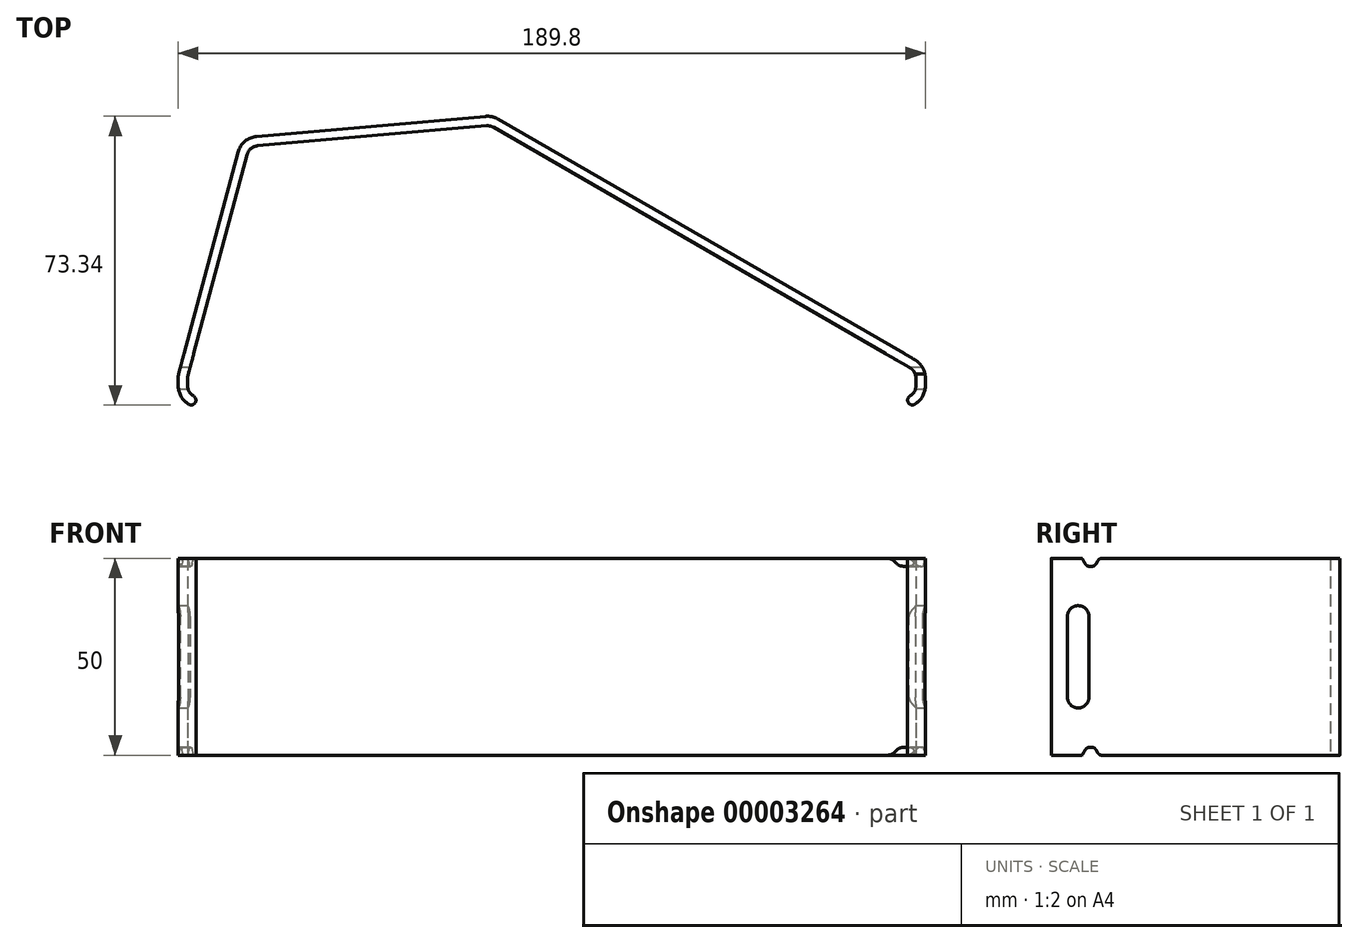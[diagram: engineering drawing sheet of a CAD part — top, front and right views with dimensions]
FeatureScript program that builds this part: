
annotation { "Feature Type Name" : "Feature", "Feature Type Description" : "" }
export const myFeature = defineFeature(function(context is Context, id is Id, definition is map)
    precondition{}
    {
        {
            var Q0;
            Q0=qCreatedBy(makeId("Top.planeOp"),FACE);
            var sketch = newSketch(context, id + "F0", { "sketchPlane" : qUnion([Q0])});
            skLineSegment(sketch, "E0", {"start": v(-74.96, 62.4) * mm, "end": v(-16.8, 67.48) * mm});
            skLineSegment(sketch, "E1", {"start": v(-13.63, 66.78) * mm, "end": v(92.2, 5.68) * mm});
            skLineSegment(sketch, "E2", {"start": v(94.9, 1) * mm, "end": v(94.9, -1) * mm});
            skLineSegment(sketch, "E3", {"start": v(92.5, -1) * mm, "end": v(92.5, 1) * mm});
            skLineSegment(sketch, "E4", {"start": v(91, 3.6) * mm, "end": v(-14.83, 64.7) * mm});
            skLineSegment(sketch, "E5", {"start": v(-16.59, 65.09) * mm, "end": v(-74.75, 60) * mm});
            skLineSegment(sketch, "E6", {"start": v(-77.39, 57.79) * mm, "end": v(-92.4, 1.78) * mm});
            skLineSegment(sketch, "E7", {"start": v(-92.5, 1) * mm, "end": v(-92.5, -1) * mm});
            skLineSegment(sketch, "E8", {"start": v(-94.9, -1) * mm, "end": v(-94.9, 1) * mm});
            skLineSegment(sketch, "E9", {"start": v(-94.72, 2.4) * mm, "end": v(-79.7, 58.4) * mm});
            skPoint(sketch, "E10.visualSharp", {"position": v(-15.1, 67.63) * mm});
            skPoint(sketch, "E11.visualSharp", {"position": v(94.9, 4.12) * mm});
            skArc(sketch, "E11.filletArc", {"start": v(94.9, 1) * mm, "mid": v(94.18, 3.7) * mm, "end": v(92.2, 5.68) * mm});
            skPoint(sketch, "E12.visualSharp", {"position": v(94.9, -8) * mm});
            skArc(sketch, "E12.filletArc", {"start": v(92.2, -5.68) * mm, "mid": v(94.18, -3.7) * mm, "end": v(94.9, -1) * mm});
            skPoint(sketch, "E13.visualSharp", {"position": v(-94.9, -5.56) * mm});
            skArc(sketch, "E13.filletArc", {"start": v(-94.9, -1) * mm, "mid": v(-94.18, -3.7) * mm, "end": v(-92.2, -5.68) * mm});
            skPoint(sketch, "E14.visualSharp", {"position": v(-94.9, 1.71) * mm});
            skArc(sketch, "E14.filletArc", {"start": v(-94.72, 2.4) * mm, "mid": v(-94.85, 1.7) * mm, "end": v(-94.9, 1) * mm});
            skPoint(sketch, "E15.visualSharp", {"position": v(-78.73, 62.06) * mm});
            skArc(sketch, "E15.filletArc", {"start": v(-74.96, 62.4) * mm, "mid": v(-77.96, 61.15) * mm, "end": v(-79.7, 58.4) * mm});
            skPoint(sketch, "E16.visualSharp", {"position": v(-15.65, 65.17) * mm});
            skArc(sketch, "E16.filletArc", {"start": v(-14.83, 64.7) * mm, "mid": v(-15.68, 65.03) * mm, "end": v(-16.59, 65.09) * mm});
            skPoint(sketch, "E17.visualSharp", {"position": v(-76.85, 59.82) * mm});
            skArc(sketch, "E17.filletArc", {"start": v(-74.75, 60) * mm, "mid": v(-76.42, 59.3) * mm, "end": v(-77.39, 57.79) * mm});
            skPoint(sketch, "E18.visualSharp", {"position": v(-92.5, 1.4) * mm});
            skArc(sketch, "E18.filletArc", {"start": v(-92.4, 1.78) * mm, "mid": v(-92.47, 1.4) * mm, "end": v(-92.5, 1) * mm});
            skPoint(sketch, "E19.visualSharp", {"position": v(92.5, 2.73) * mm});
            skArc(sketch, "E19.filletArc", {"start": v(92.5, 1) * mm, "mid": v(92.1, 2.5) * mm, "end": v(91, 3.6) * mm});
            skPoint(sketch, "E20.visualSharp", {"position": v(92.5, -2.9) * mm});
            skArc(sketch, "E20.filletArc", {"start": v(91, -3.6) * mm, "mid": v(92.1, -2.5) * mm, "end": v(92.5, -1) * mm});
            skPoint(sketch, "E21.visualSharp", {"position": v(-92.5, -3) * mm});
            skArc(sketch, "E21.filletArc", {"start": v(-92.5, -1) * mm, "mid": v(-92.1, -2.5) * mm, "end": v(-91, -3.6) * mm});
            skLineSegment(sketch, "E22", {"start": v(92.5, 0) * mm, "end": v(-92.5, 0) * mm, "construction": true});
            skArc(sketch, "E23", {"start": v(-92.2, -5.68) * mm, "mid": v(-90.56, -5.24) * mm, "end": v(-91, -3.6) * mm});
            skArc(sketch, "E24", {"start": v(91, -3.6) * mm, "mid": v(90.56, -5.24) * mm, "end": v(92.2, -5.68) * mm});
            skArc(sketch, "E25", {"start": v(-13.63, 66.78) * mm, "mid": v(-15.16, 67.37) * mm, "end": v(-16.8, 67.48) * mm});
            skLineSegment(sketch, "E26", {"start": v(-89.5, -1) * mm, "end": v(-91.6, -4.64) * mm, "construction": true});
            skLineSegment(sketch, "E27", {"start": v(89.5, -1) * mm, "end": v(91.6, -4.64) * mm, "construction": true});
            skSolve(sketch);
        }
        {
            var Q0;
            Q0 = qSketchRegion(id + "F0", true);
            extrude(context, id + "F1", {"entities" : qUnion([Q0]), "endBound" : BoundingType.SYMMETRIC, "depth" : 50 * mm});
        }
        {
            var Q0;
            Q0=qCreatedBy(makeId("Right.planeOp"),FACE);
            var sketch = newSketch(context, id + "F2", { "sketchPlane" : qUnion([Q0])});
            skLineSegment(sketch, "E28", {"start": v(3.75, 10.25) * mm, "end": v(3.75, -10.25) * mm});
            skLineSegment(sketch, "E29", {"start": v(-1.75, 10.25) * mm, "end": v(-1.75, -10.25) * mm});
            skArc(sketch, "E30", {"start": v(3.75, 10.25) * mm, "mid": v(1, 13) * mm, "end": v(-1.75, 10.25) * mm});
            skArc(sketch, "E31", {"start": v(3.75, -10.25) * mm, "mid": v(1, -13) * mm, "end": v(-1.75, -10.25) * mm});
            skLineSegment(sketch, "E32", {"start": v(1, 10.25) * mm, "end": v(1, -10.25) * mm, "construction": true});
            skLineSegment(sketch, "E33", {"start": v(1, 0) * mm, "end": v(0, 0) * mm, "construction": true});
            skLineSegment(sketch, "E34", {"start": v(1, 13) * mm, "end": v(1, 25) * mm, "construction": true});
            skSolve(sketch);
        }
        {
            var Q0;
            Q0 = qSketchRegion(id + "F2", true);
            extrude(context, id + "F3", {"entities" : qUnion([Q0]), "operationType" : NewBodyOperationType.REMOVE, "endBound" : BoundingType.THROUGH_ALL, "oppositeDirection" : true, "depth" : 25 * mm, "hasSecondDirection" : true, "secondDirectionBound" : SecondDirectionBoundingType.THROUGH_ALL, "secondDirectionOppositeDirection" : false, "secondDirectionDepth" : 25 * mm});
        }
        {
            var Q0;
            Q0=qCreatedBy(makeId("Right.planeOp"),FACE);
            var sketch = newSketch(context, id + "F4", { "sketchPlane" : qUnion([Q0])});
            skLineSegment(sketch, "E35", {"start": v(2, 25) * mm, "end": v(2, 25) * mm});
            skLineSegment(sketch, "E36", {"start": v(2, 25) * mm, "end": v(3.15, 23) * mm});
            skLineSegment(sketch, "E37", {"start": v(3.15, 23) * mm, "end": v(5.15, 23) * mm});
            skLineSegment(sketch, "E38", {"start": v(5.15, 23) * mm, "end": v(6.3, 25) * mm});
            skLineSegment(sketch, "E39", {"start": v(6.3, 25) * mm, "end": v(2, 25) * mm});
            skLineSegment(sketch, "E40", {"start": v(0, 0) * mm, "end": v(-15.35, 0) * mm, "construction": true});
            skLineSegment(sketch, "E41.MirrorCS", {"start": v(6.3, -25) * mm, "end": v(2, -25) * mm});
            skLineSegment(sketch, "E42.MirrorCS", {"start": v(3.15, -23) * mm, "end": v(5.15, -23) * mm});
            skLineSegment(sketch, "E43.MirrorCS", {"start": v(5.15, -23) * mm, "end": v(6.3, -25) * mm});
            skLineSegment(sketch, "E44.MirrorCS", {"start": v(2, -25) * mm, "end": v(2, -25) * mm});
            skLineSegment(sketch, "E45.MirrorCS", {"start": v(2, -25) * mm, "end": v(3.15, -23) * mm});
            skLineSegment(sketch, "E46", {"start": v(0, 0) * mm, "end": v(2, 0) * mm, "construction": true});
            skLineSegment(sketch, "E47", {"start": v(2, 25) * mm, "end": v(2, -25) * mm, "construction": true});
            skSolve(sketch);
        }
        {
            var Q0;
            Q0 = qSketchRegion(id + "F4", true);
            extrude(context, id + "F5", {"entities" : qUnion([Q0]), "operationType" : NewBodyOperationType.REMOVE, "endBound" : BoundingType.THROUGH_ALL, "oppositeDirection" : true, "depth" : 25 * mm, "hasSecondDirection" : true, "secondDirectionBound" : SecondDirectionBoundingType.THROUGH_ALL, "secondDirectionOppositeDirection" : false, "secondDirectionDepth" : 25 * mm});
        }
        {
            var Q0;
            Q0=makeQuery(id+"F5.boolean.opBoolean","COPY",EDGE,{"disambiguationData":[OD(0.0)],"derivedFrom":makeQuery(id+"F5.opExtrude","SWEPT_EDGE",EDGE,{"disambiguationData":[OSD([sQuery(id+"F4.wireOp",EDGE,"E36"),sQuery(id+"F4.wireOp",EDGE,"E39")])]})});
            var Q1;
            Q1=makeQuery(id+"F5.boolean.opBoolean","COPY",EDGE,{"disambiguationData":[OD(1.0)],"derivedFrom":makeQuery(id+"F5.opExtrude","SWEPT_EDGE",EDGE,{"disambiguationData":[OSD([sQuery(id+"F4.wireOp",EDGE,"E36"),sQuery(id+"F4.wireOp",EDGE,"E39")])]})});
            var Q2;
            Q2=makeQuery(id+"F5.boolean.opBoolean","COPY",EDGE,{"disambiguationData":[OD(0.0)],"derivedFrom":makeQuery(id+"F5.opExtrude","SWEPT_EDGE",EDGE,{"disambiguationData":[OSD([sQuery(id+"F4.wireOp",EDGE,"E38"),sQuery(id+"F4.wireOp",EDGE,"E39")])]})});
            var Q3;
            Q3=makeQuery(id+"F5.boolean.opBoolean","COPY",EDGE,{"disambiguationData":[OD(1.0)],"derivedFrom":makeQuery(id+"F5.opExtrude","SWEPT_EDGE",EDGE,{"disambiguationData":[OSD([sQuery(id+"F4.wireOp",EDGE,"E38"),sQuery(id+"F4.wireOp",EDGE,"E39")])]})});
            var Q4;
            Q4=makeQuery(id+"F5.boolean.opBoolean","COPY",EDGE,{"disambiguationData":[OD(0.0)],"derivedFrom":makeQuery(id+"F5.opExtrude","SWEPT_EDGE",EDGE,{"disambiguationData":[OSD([sQuery(id+"F4.wireOp",EDGE,"E41.MirrorCS"),sQuery(id+"F4.wireOp",EDGE,"E43.MirrorCS")])]})});
            var Q5;
            Q5=makeQuery(id+"F5.boolean.opBoolean","COPY",EDGE,{"disambiguationData":[OD(0.0)],"derivedFrom":makeQuery(id+"F5.opExtrude","SWEPT_EDGE",EDGE,{"disambiguationData":[OSD([sQuery(id+"F4.wireOp",EDGE,"E41.MirrorCS"),sQuery(id+"F4.wireOp",EDGE,"E45.MirrorCS")])]})});
            var Q6;
            Q6=makeQuery(id+"F5.boolean.opBoolean","COPY",EDGE,{"disambiguationData":[OD(1.0)],"derivedFrom":makeQuery(id+"F5.opExtrude","SWEPT_EDGE",EDGE,{"disambiguationData":[OSD([sQuery(id+"F4.wireOp",EDGE,"E41.MirrorCS"),sQuery(id+"F4.wireOp",EDGE,"E43.MirrorCS")])]})});
            var Q7;
            Q7=makeQuery(id+"F5.boolean.opBoolean","COPY",EDGE,{"disambiguationData":[OD(1.0)],"derivedFrom":makeQuery(id+"F5.opExtrude","SWEPT_EDGE",EDGE,{"disambiguationData":[OSD([sQuery(id+"F4.wireOp",EDGE,"E41.MirrorCS"),sQuery(id+"F4.wireOp",EDGE,"E45.MirrorCS")])]})});
            var Q8;
            Q8=makeQuery(id+"F5.boolean.opBoolean","COPY",EDGE,{"disambiguationData":[OD(1.0)],"derivedFrom":makeQuery(id+"F5.opExtrude","SWEPT_EDGE",EDGE,{"disambiguationData":[OSD([sQuery(id+"F4.wireOp",EDGE,"E36"),sQuery(id+"F4.wireOp",EDGE,"E37")])]})});
            var Q9;
            Q9=makeQuery(id+"F5.boolean.opBoolean","COPY",EDGE,{"disambiguationData":[OD(0.0)],"derivedFrom":makeQuery(id+"F5.opExtrude","SWEPT_EDGE",EDGE,{"disambiguationData":[OSD([sQuery(id+"F4.wireOp",EDGE,"E37"),sQuery(id+"F4.wireOp",EDGE,"E38")])]})});
            var Q10;
            Q10=makeQuery(id+"F5.boolean.opBoolean","COPY",EDGE,{"disambiguationData":[OD(1.0)],"derivedFrom":makeQuery(id+"F5.opExtrude","SWEPT_EDGE",EDGE,{"disambiguationData":[OSD([sQuery(id+"F4.wireOp",EDGE,"E37"),sQuery(id+"F4.wireOp",EDGE,"E38")])]})});
            var Q11;
            Q11=makeQuery(id+"F5.boolean.opBoolean","COPY",EDGE,{"disambiguationData":[OD(0.0)],"derivedFrom":makeQuery(id+"F5.opExtrude","SWEPT_EDGE",EDGE,{"disambiguationData":[OSD([sQuery(id+"F4.wireOp",EDGE,"E36"),sQuery(id+"F4.wireOp",EDGE,"E37")])]})});
            var Q12;
            Q12=makeQuery(id+"F5.boolean.opBoolean","COPY",EDGE,{"disambiguationData":[OD(1.0)],"derivedFrom":makeQuery(id+"F5.opExtrude","SWEPT_EDGE",EDGE,{"disambiguationData":[OSD([sQuery(id+"F4.wireOp",EDGE,"E42.MirrorCS"),sQuery(id+"F4.wireOp",EDGE,"E43.MirrorCS")])]})});
            var Q13;
            Q13=makeQuery(id+"F5.boolean.opBoolean","COPY",EDGE,{"disambiguationData":[OD(0.0)],"derivedFrom":makeQuery(id+"F5.opExtrude","SWEPT_EDGE",EDGE,{"disambiguationData":[OSD([sQuery(id+"F4.wireOp",EDGE,"E42.MirrorCS"),sQuery(id+"F4.wireOp",EDGE,"E45.MirrorCS")])]})});
            var Q14;
            Q14=makeQuery(id+"F5.boolean.opBoolean","COPY",EDGE,{"disambiguationData":[OD(0.0)],"derivedFrom":makeQuery(id+"F5.opExtrude","SWEPT_EDGE",EDGE,{"disambiguationData":[OSD([sQuery(id+"F4.wireOp",EDGE,"E42.MirrorCS"),sQuery(id+"F4.wireOp",EDGE,"E43.MirrorCS")])]})});
            var Q15;
            Q15=makeQuery(id+"F5.boolean.opBoolean","COPY",EDGE,{"disambiguationData":[OD(1.0)],"derivedFrom":makeQuery(id+"F5.opExtrude","SWEPT_EDGE",EDGE,{"disambiguationData":[OSD([sQuery(id+"F4.wireOp",EDGE,"E42.MirrorCS"),sQuery(id+"F4.wireOp",EDGE,"E45.MirrorCS")])]})});
            fillet(context, id + "F6", {"entities" : qUnion([Q0, Q1, Q2, Q3, Q4, Q5, Q6, Q7, Q8, Q9, Q10, Q11, Q12, Q13, Q14, Q15]), "radius" : 1.5 * mm, "tangentPropagation" : true, "rho" : .6, "crossSection" : FilletCrossSection.CONIC, "allowEdgeOverflow" : false});
        }
    });
